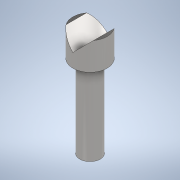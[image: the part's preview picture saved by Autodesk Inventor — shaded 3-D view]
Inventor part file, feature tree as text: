
AUTODESK INVENTOR PART (.ipt)
format: ipt  version: 2020 (Build 240168000, 168)  size: 130,048 bytes
history: native  units: in
note: dims shown in document units (in); Inventor stores cm internally (conversion verified against a paired STEP export)
features: sketch x2, projected_geometry x2, revolve x1, extrude x1
ambient origin geometry x8: Origin, YZ Plane, XZ Plane, XY Plane, X Axis, Y Axis, Z Axis, Center Point
bodies: Solid1 (feature_tree)
feature tree (6):
  revolve  "Revolution1"  [1 undecoded]
  extrude  "Extrusion1"  Depth=2.0in
  sketch  "Sketch1"  dims[d0=0.373in d1=0.5in]
  sketch  "Sketch3"  dims[d2=0.625in d3=2.0in d4=90.0deg d5=0.0625in d6=0.0625in d7=45.0deg d8=45.0deg d9=1.0in d10=0.0in]
  projected_geometry  "Projected Loop1"
  projected_geometry  "Project Cut Edges1"
note: 1 required parameter value undecoded (feature->parameter linkage not recoverable at this tier; creation-order binding heuristic only, values carry confidence <= 0.55)
